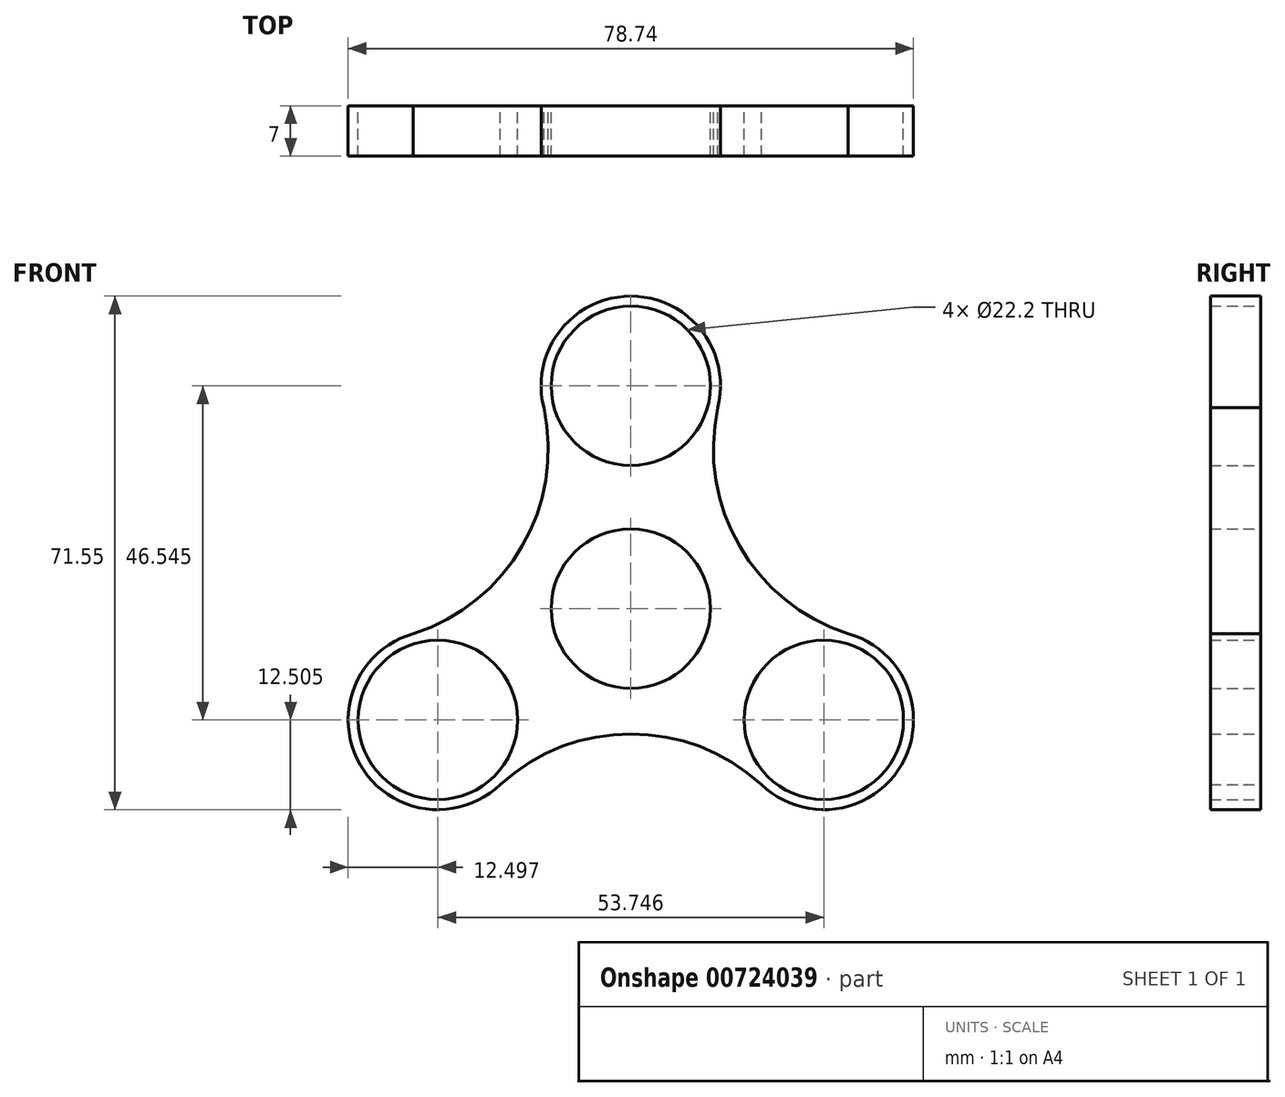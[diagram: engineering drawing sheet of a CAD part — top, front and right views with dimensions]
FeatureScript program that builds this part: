
annotation { "Feature Type Name" : "Feature", "Feature Type Description" : "" }
export const myFeature = defineFeature(function(context is Context, id is Id, definition is map)
    precondition{}
    {
        {
            var Q0;
            Q0=qCreatedBy(makeId("Front.planeOp"),FACE);
            var sketch = newSketch(context, id + "F0", { "sketchPlane" : qUnion([Q0])});
            skCircle(sketch, "E0", {"center": v(0, 0) * mm, "radius": 11.1 * mm});
            skCircle(sketch, "E1", {"center": v(0, 31.03) * mm, "radius": 11.1 * mm});
            skCircle(sketch, "E2.1.0", {"center": v(-26.87, -15.52) * mm, "radius": 11.1 * mm});
            skCircle(sketch, "E2.2.0", {"center": v(26.87, -15.52) * mm, "radius": 11.1 * mm});
            skArc(sketch, "E3", {"start": v(12.12, 27.98) * mm, "mid": v(0, 43.53) * mm, "end": v(-12.12, 27.98) * mm});
            skArc(sketch, "E4", {"start": v(-30.3, -3.5) * mm, "mid": v(-37.7, -21.77) * mm, "end": v(-18.17, -24.49) * mm});
            skArc(sketch, "E5", {"start": v(18.17, -24.49) * mm, "mid": v(37.7, -21.77) * mm, "end": v(30.3, -3.5) * mm});
            skArc(sketch, "E6", {"start": v(12.24, 28.51) * mm, "mid": v(15.12, 8.73) * mm, "end": v(30.81, -3.65) * mm});
            skArc(sketch, "E7", {"start": v(18.57, -24.86) * mm, "mid": v(0, -17.46) * mm, "end": v(-18.57, -24.86) * mm});
            skArc(sketch, "E8", {"start": v(-30.81, -3.65) * mm, "mid": v(-15.12, 8.73) * mm, "end": v(-12.24, 28.51) * mm});
            skSolve(sketch);
        }
        {
            var Q0;
            Q0 = qSketchRegion(id + "F0", true);
            extrude(context, id + "F1", {"entities" : qUnion([Q0]), "depth" : 7 * mm, "offsetDistance" : 25 * mm});
        }
    });
